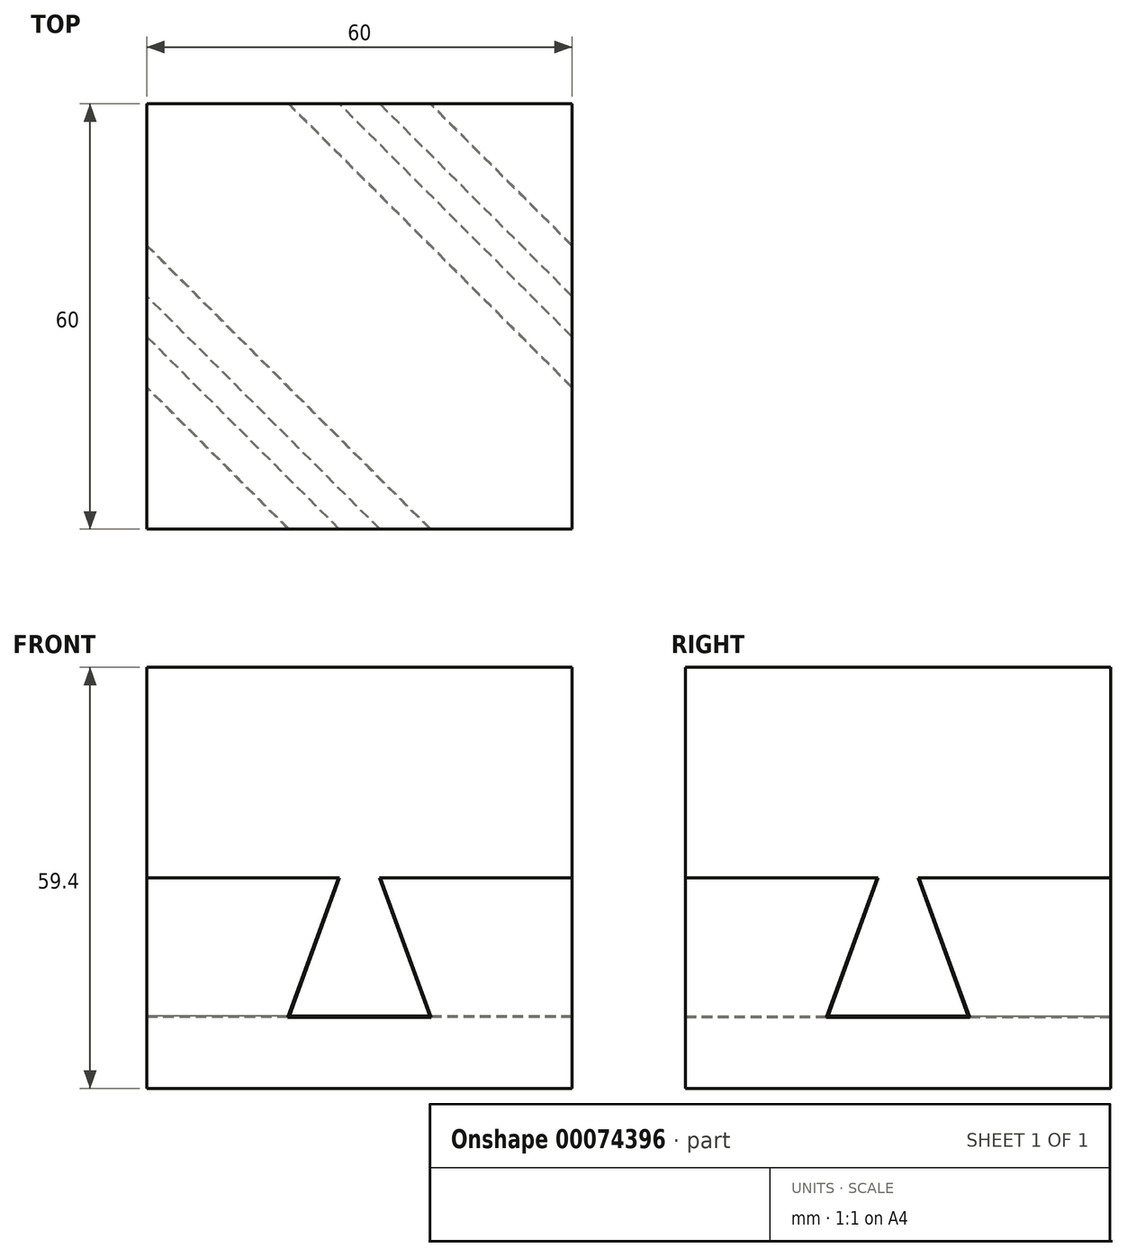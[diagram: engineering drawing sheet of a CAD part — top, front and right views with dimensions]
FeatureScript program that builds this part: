
annotation { "Feature Type Name" : "Feature", "Feature Type Description" : "" }
export const myFeature = defineFeature(function(context is Context, id is Id, definition is map)
    precondition{}
    {
        {
            var Q0;
            Q0=qCreatedBy(makeId("Top.planeOp"),FACE);
            var sketch = newSketch(context, id + "F0", { "sketchPlane" : qUnion([Q0])});
            skLineSegment(sketch, "E0.bottom", {"start": v(0, 0) * mm, "end": v(60, 0) * mm});
            skLineSegment(sketch, "E0.top", {"start": v(0, 60) * mm, "end": v(60, 60) * mm});
            skLineSegment(sketch, "E0.left", {"start": v(0, 0) * mm, "end": v(0, 60) * mm});
            skLineSegment(sketch, "E0.right", {"start": v(60, 0) * mm, "end": v(60, 60) * mm});
            skSolve(sketch);
        }
        {
            var Q0;
            Q0 = qSketchRegion(id + "F0", true);
            extrude(context, id + "F1", {"entities" : qUnion([Q0]), "depth" : 29.7 * mm});
        }
        {
            var Q0;
            Q0=makeQuery(id+"F1.opExtrude","SWEPT_FACE",FACE,{"disambiguationData":[OSD([sQuery(id+"F0.wireOp",EDGE,"E0.bottom")])]});
            var sketch = newSketch(context, id + "F2", { "sketchPlane" : qUnion([Q0])});
            skLineSegment(sketch, "E1", {"start": v(27.07, 29.7) * mm, "end": v(19.9, 10) * mm});
            skLineSegment(sketch, "E2", {"start": v(19.9, 10) * mm, "end": v(40.1, 10) * mm});
            skLineSegment(sketch, "E3", {"start": v(40.1, 10) * mm, "end": v(32.93, 29.7) * mm});
            skLineSegment(sketch, "E4", {"start": v(32.93, 29.7) * mm, "end": v(27.07, 29.7) * mm});
            skLineSegment(sketch, "E5", {"start": v(30, 29.7) * mm, "end": v(30, 0) * mm, "construction": true});
            skSolve(sketch);
        }
        {
            var Q0;
            Q0=makeQuery(id+"F1.opExtrude","CAP_FACE",FACE,{"disambiguationData":[OSD([sQuery(id+"F0.wireOp",EDGE,"E0.bottom"),sQuery(id+"F0.wireOp",EDGE,"E0.top"),sQuery(id+"F0.wireOp",EDGE,"E0.left"),sQuery(id+"F0.wireOp",EDGE,"E0.right")])],"isStart":false});
            var sketch = newSketch(context, id + "F3", { "sketchPlane" : qUnion([Q0])});
            skLineSegment(sketch, "E6", {"start": v(60, 0) * mm, "end": v(0, 60) * mm});
            skSolve(sketch);
        }
        {
            var Q0;
            Q0 = qSketchRegion(id + "F2", true);
            var Q1;
            Q1 = qConstructionFilter(qBodyType(qCreatedBy(id + "F3" ,EDGE), BodyType.WIRE), ConstructionObject.NO);
            sweep(context, id + "F4", {"operationType" : NewBodyOperationType.REMOVE, "profiles" : qUnion([Q0]), "path" : qUnion([Q1])});
        }
        {
            var Q0;
            Q0=makeQuery(id+"F1.opExtrude","SWEPT_FACE",FACE,{"disambiguationData":[OSD([sQuery(id+"F0.wireOp",EDGE,"E0.right")])]});
            var sketch = newSketch(context, id + "F5", { "sketchPlane" : qUnion([Q0])});
            skLineSegment(sketch, "E7", {"start": v(27.07, 29.7) * mm, "end": v(19.9, 10) * mm});
            skLineSegment(sketch, "E8", {"start": v(19.9, 10) * mm, "end": v(40.1, 10) * mm});
            skLineSegment(sketch, "E9", {"start": v(40.1, 10) * mm, "end": v(32.93, 29.7) * mm});
            skLineSegment(sketch, "E10", {"start": v(32.93, 29.7) * mm, "end": v(27.07, 29.7) * mm});
            skLineSegment(sketch, "E11", {"start": v(30, 26.26) * mm, "end": v(30, -3.44) * mm, "construction": true});
            skSolve(sketch);
        }
        {
            var Q0;
            Q0=makeQuery(id+"F5.imprint","IMPRINT",FACE,{"disambiguationData":[TD([[makeQuery(id+"F5.imprint","IMPRINT",EDGE,{"derivedFrom":sQuery(id+"F5.wireOp",EDGE,"E7")}),1.0]])]});
            var Q1;
            Q1 = qConstructionFilter(qBodyType(qCreatedBy(id + "F3" ,EDGE), BodyType.WIRE), ConstructionObject.NO);
            sweep(context, id + "F6", {"operationType" : NewBodyOperationType.REMOVE, "profiles" : qUnion([Q0]), "path" : qUnion([Q1])});
        }
        {
            var Q0;
            {var subQ0=sQuery(id+"F0.wireOp",EDGE,"E0.right");var subQ4=sQuery(id+"F0.wireOp",EDGE,"E0.left");var subQ6=sQuery(id+"F0.wireOp",EDGE,"E0.top");var subQ7=makeQuery(id+"F1.opExtrude","SWEPT_FACE",FACE,{"disambiguationData":[OSD([subQ6])]});var subQ8=sQuery(id+"F0.wireOp",EDGE,"E0.bottom");var subQ9=makeQuery(id+"F1.opExtrude","SWEPT_FACE",FACE,{"disambiguationData":[OSD([subQ8])]});Q0=makeQuery(id+"F6.boolean.opBoolean","SPLIT",FACE,{"disambiguationData":[TD([subQ9])],"derivedFrom":makeQuery(id+"F4.boolean.opBoolean","SPLIT",FACE,{"disambiguationData":[TD([subQ7])],"derivedFrom":makeQuery(id+"F1.opExtrude","CAP_FACE",FACE,{"disambiguationData":[OSD([subQ8,subQ6,subQ4,subQ0])],"isStart":false})})});}
            var sketch = newSketch(context, id + "F7", { "sketchPlane" : qUnion([Q0])});
            skLineSegment(sketch, "E12.bottom", {"start": v(0, 0) * mm, "end": v(60, 0) * mm});
            skLineSegment(sketch, "E12.top", {"start": v(0, 60) * mm, "end": v(60, 60) * mm});
            skLineSegment(sketch, "E12.left", {"start": v(0, 0) * mm, "end": v(0, 60) * mm});
            skLineSegment(sketch, "E12.right", {"start": v(60, 0) * mm, "end": v(60, 60) * mm});
            skSolve(sketch);
        }
        {
            var Q0;
            Q0 = qSketchRegion(id + "F7", true);
            extrude(context, id + "F8", {"entities" : qUnion([Q0]), "depth" : 29.7 * mm});
        }
        {
            var Q0;
            Q0=makeQuery(id+"F8.opExtrude","SWEPT_FACE",FACE,{"disambiguationData":[OSD([sQuery(id+"F7.wireOp",EDGE,"E12.right")])]});
            var sketch = newSketch(context, id + "F9", { "sketchPlane" : qUnion([Q0])});
            skLineSegment(sketch, "E13", {"start": v(27.2, 29.7) * mm, "end": v(20.1, 10.2) * mm});
            skLineSegment(sketch, "E14", {"start": v(20.1, 10.2) * mm, "end": v(39.9, 10.2) * mm});
            skLineSegment(sketch, "E15", {"start": v(39.9, 10.2) * mm, "end": v(32.8, 29.7) * mm});
            skLineSegment(sketch, "E16", {"start": v(32.8, 29.7) * mm, "end": v(30.87, 29.7) * mm});
            skLineSegment(sketch, "E17.top", {"start": v(28.77, 37.01) * mm, "end": v(30.87, 37.01) * mm});
            skLineSegment(sketch, "E17.left", {"start": v(28.77, 29.7) * mm, "end": v(28.77, 37.01) * mm});
            skLineSegment(sketch, "E17.right", {"start": v(30.87, 29.7) * mm, "end": v(30.87, 37.01) * mm});
            skLineSegment(sketch, "E18.trimOffspring", {"start": v(28.77, 29.7) * mm, "end": v(27.2, 29.7) * mm});
            skLineSegment(sketch, "E19", {"start": v(30, 29.7) * mm, "end": v(30, 0) * mm, "construction": true});
            skSolve(sketch);
        }
        {
            var Q0;
            Q0=makeQuery(id+"F9.imprint","IMPRINT",FACE,{"disambiguationData":[TD([[makeQuery(id+"F9.imprint","IMPRINT",EDGE,{"derivedFrom":sQuery(id+"F9.wireOp",EDGE,"E17.top")}),-1.0]])]});
            var Q1;
            Q1=makeQuery(id+"F9.imprint","IMPRINT",FACE,{"disambiguationData":[TD([[makeQuery(id+"F9.imprint","IMPRINT",EDGE,{"derivedFrom":sQuery(id+"F9.wireOp",EDGE,"E13")}),1.0]])]});
            var Q2;
            Q2 = qConstructionFilter(qBodyType(qCreatedBy(id + "F3" ,EDGE), BodyType.WIRE), ConstructionObject.NO);
            sweep(context, id + "F10", {"operationType" : NewBodyOperationType.ADD, "profiles" : qUnion([Q0, Q1]), "path" : qUnion([Q2])});
        }
        {
            var Q0;
            Q0=makeQuery(id+"F1.opExtrude","SWEPT_FACE",FACE,{"disambiguationData":[OSD([sQuery(id+"F0.wireOp",EDGE,"E0.bottom")])]});
            var sketch = newSketch(context, id + "F11", { "sketchPlane" : qUnion([Q0])});
            skLineSegment(sketch, "E20", {"start": v(27.2, 29.7) * mm, "end": v(20.1, 10.2) * mm});
            skLineSegment(sketch, "E21", {"start": v(20.1, 10.2) * mm, "end": v(39.9, 10.2) * mm});
            skLineSegment(sketch, "E22", {"start": v(39.9, 10.2) * mm, "end": v(32.8, 29.7) * mm});
            skLineSegment(sketch, "E23", {"start": v(32.8, 29.7) * mm, "end": v(27.2, 29.7) * mm});
            skLineSegment(sketch, "E24", {"start": v(30, 0) * mm, "end": v(30, 32.33) * mm, "construction": true});
            skSolve(sketch);
        }
        {
            var Q0;
            Q0 = qSketchRegion(id + "F11", true);
            var Q1;
            Q1 = qConstructionFilter(qBodyType(qCreatedBy(id + "F3" ,EDGE), BodyType.WIRE), ConstructionObject.NO);
            sweep(context, id + "F12", {"operationType" : NewBodyOperationType.ADD, "profiles" : qUnion([Q0]), "path" : qUnion([Q1])});
        }
        {
            var Q0;
            Q0=makeQuery(id+"F8.opExtrude","CAP_FACE",FACE,{"disambiguationData":[OSD([sQuery(id+"F7.wireOp",EDGE,"E12.bottom"),sQuery(id+"F7.wireOp",EDGE,"E12.top"),sQuery(id+"F7.wireOp",EDGE,"E12.left"),sQuery(id+"F7.wireOp",EDGE,"E12.right")])],"isStart":false});
            var sketch = newSketch(context, id + "F13", { "sketchPlane" : qUnion([Q0])});
            skLineSegment(sketch, "E25", {"start": v(0, 0) * mm, "end": v(0, 60) * mm});
            skLineSegment(sketch, "E26", {"start": v(0, 60) * mm, "end": v(60, 60) * mm});
            skLineSegment(sketch, "E27", {"start": v(60, 60) * mm, "end": v(60, 121.13) * mm});
            skLineSegment(sketch, "E28", {"start": v(60, 121.13) * mm, "end": v(-99, 121.13) * mm});
            skLineSegment(sketch, "E29", {"start": v(-99, 121.13) * mm, "end": v(-99, 0) * mm});
            skLineSegment(sketch, "E30", {"start": v(-99, 0) * mm, "end": v(0, 0) * mm});
            skSolve(sketch);
        }
        {
            var Q0;
            Q0=makeQuery(id+"F13.imprint","IMPRINT",FACE,{"disambiguationData":[TD([[makeQuery(id+"F13.imprint","IMPRINT",EDGE,{"derivedFrom":sQuery(id+"F13.wireOp",EDGE,"E25")}),1.0]])]});
            var Q1;
            Q1=makeQuery(id+"F1.opExtrude","CAP_FACE",FACE,{"disambiguationData":[OSD([sQuery(id+"F0.wireOp",EDGE,"E0.bottom"),sQuery(id+"F0.wireOp",EDGE,"E0.top"),sQuery(id+"F0.wireOp",EDGE,"E0.left"),sQuery(id+"F0.wireOp",EDGE,"E0.right")])],"isStart":true});
            extrude(context, id + "F14", {"entities" : qUnion([Q0]), "operationType" : NewBodyOperationType.REMOVE, "endBound" : BoundingType.UP_TO_SURFACE, "oppositeDirection" : true, "endBoundEntityFace" : qUnion([Q1]), "depth" : 25 * mm});
        }
    });
